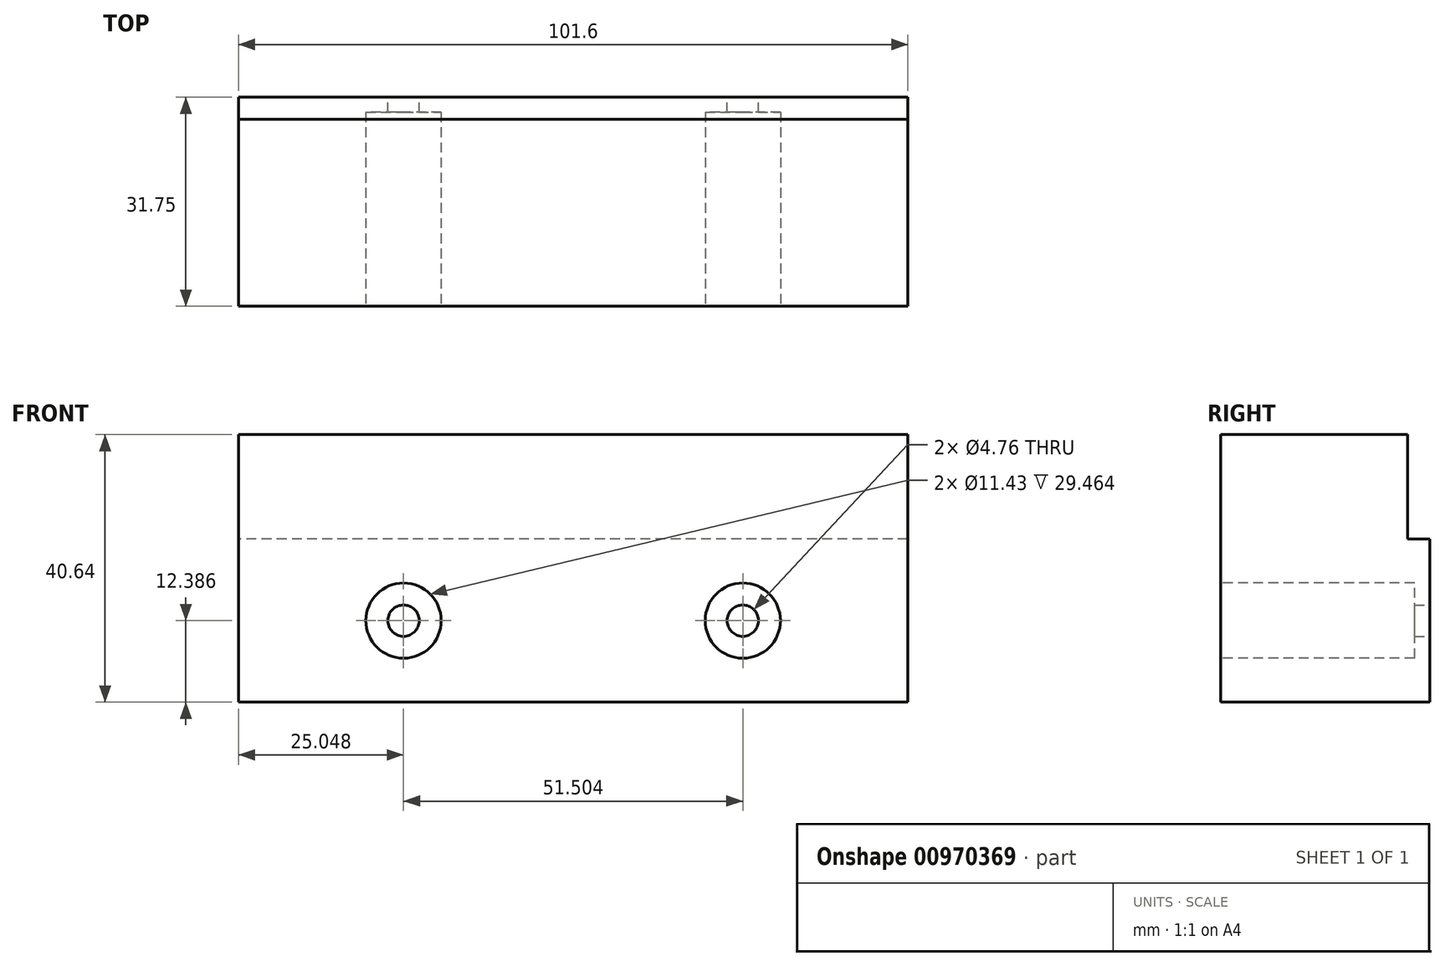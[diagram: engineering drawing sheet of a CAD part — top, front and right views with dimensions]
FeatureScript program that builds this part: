
annotation { "Feature Type Name" : "Feature", "Feature Type Description" : "" }
export const myFeature = defineFeature(function(context is Context, id is Id, definition is map)
    precondition{}
    {
        {
            var Q0;
            Q0=qCreatedBy(makeId("Right.planeOp"),FACE);
            var sketch = newSketch(context, id + "F0", { "sketchPlane" : qUnion([Q0])});
            skLineSegment(sketch, "E0", {"start": v(0, -15.32) * mm, "end": v(-3, -15.32) * mm});
            skLineSegment(sketch, "E1", {"start": v(-3, -15.32) * mm, "end": v(-3, -55.96) * mm});
            skLineSegment(sketch, "E2", {"start": v(-3, -55.96) * mm, "end": v(3.35, -55.96) * mm});
            skLineSegment(sketch, "E3", {"start": v(3.35, -55.96) * mm, "end": v(3.35, -31.2) * mm});
            skLineSegment(sketch, "E4", {"start": v(3.35, -31.2) * mm, "end": v(0, -31.2) * mm});
            skLineSegment(sketch, "E5", {"start": v(0, -31.2) * mm, "end": v(0, -15.32) * mm});
            skSolve(sketch);
        }
        {
            var Q0;
            Q0=qSketchRegion(id+"F0",true);
            extrude(context, id + "F1", {"entities" : qUnion([Q0]), "depth" : 101.6 * mm});
        }
        {
            var Q0;
            Q0=makeQuery(id+"F1.opExtrude","SWEPT_FACE",FACE,{"disambiguationData":[OSD([sQuery(id+"F0.wireOp",EDGE,"E3")])]});
            var sketch = newSketch(context, id + "F2", { "sketchPlane" : qUnion([Q0])});
            skLineSegment(sketch, "E6", {"start": v(-50.8, -31.2) * mm, "end": v(-50.8, -55.96) * mm, "construction": true});
            skCircle(sketch, "E7", {"center": v(-76.55, -43.57) * mm, "radius": 2.38 * mm});
            skPoint(sketch, "E7.centerSnap0", {"position": v(-101.6, -43.57) * mm});
            skCircle(sketch, "E8.MirrorC", {"center": v(-25.05, -43.57) * mm, "radius": 2.38 * mm});
            skSolve(sketch);
        }
        {
            var Q0;
            Q0=qSketchRegion(id+"F2",true);
            extrude(context, id + "F3", {"entities" : qUnion([Q0]), "operationType" : NewBodyOperationType.REMOVE, "endBound" : BoundingType.UP_TO_NEXT, "oppositeDirection" : true, "depth" : 25.4 * mm});
        }
        {
            var Q0;
            Q0=makeQuery(id+"F1.opExtrude","SWEPT_FACE",FACE,{"disambiguationData":[OSD([sQuery(id+"F0.wireOp",EDGE,"E1")])]});
            var sketch = newSketch(context, id + "F4", { "sketchPlane" : qUnion([Q0])});
            skCircle(sketch, "E9", {"center": v(25.05, -43.57) * mm, "radius": 5.72 * mm});
            skCircle(sketch, "E10", {"center": v(76.55, -43.57) * mm, "radius": 5.72 * mm});
            skSolve(sketch);
        }
        {
            var Q0;
            Q0=qSketchRegion(id+"F4",true);
            extrude(context, id + "F5", {"entities" : qUnion([Q0]), "operationType" : NewBodyOperationType.REMOVE, "oppositeDirection" : true, "depth" : 4.06 * mm});
        }
        {
            var Q0;
            Q0=makeQuery(id+"F1.opExtrude","SWEPT_FACE",FACE,{"disambiguationData":[OSD([sQuery(id+"F0.wireOp",EDGE,"E1")])]});
            extrude(context, id + "F6", {"entities" : qUnion([Q0]), "operationType" : NewBodyOperationType.ADD, "depth" : 25.4 * mm, "offsetDistance" : 25.4 * mm});
        }
        {
            var Q0;
            {var subQ0=sQuery(id+"F0.wireOp",EDGE,"E0");Q0=makeQuery(id+"F6.boolean.opBoolean","MERGE",FACE,{"derivedFrom":[makeQuery(id+"F1.opExtrude","SWEPT_FACE",FACE,{"disambiguationData":[OSD([subQ0])]}),makeQuery(id+"F6.opExtrude","SWEPT_FACE",FACE,{"disambiguationData":[OSD([subQ0,sQuery(id+"F0.wireOp",EDGE,"E1")])]})]});}
            extrude(context, id + "F7", {"entities" : qUnion([Q0]), "operationType" : NewBodyOperationType.REMOVE, "depth" : 23.8 * mm, "offsetDistance" : 25.4 * mm});
        }
    });
